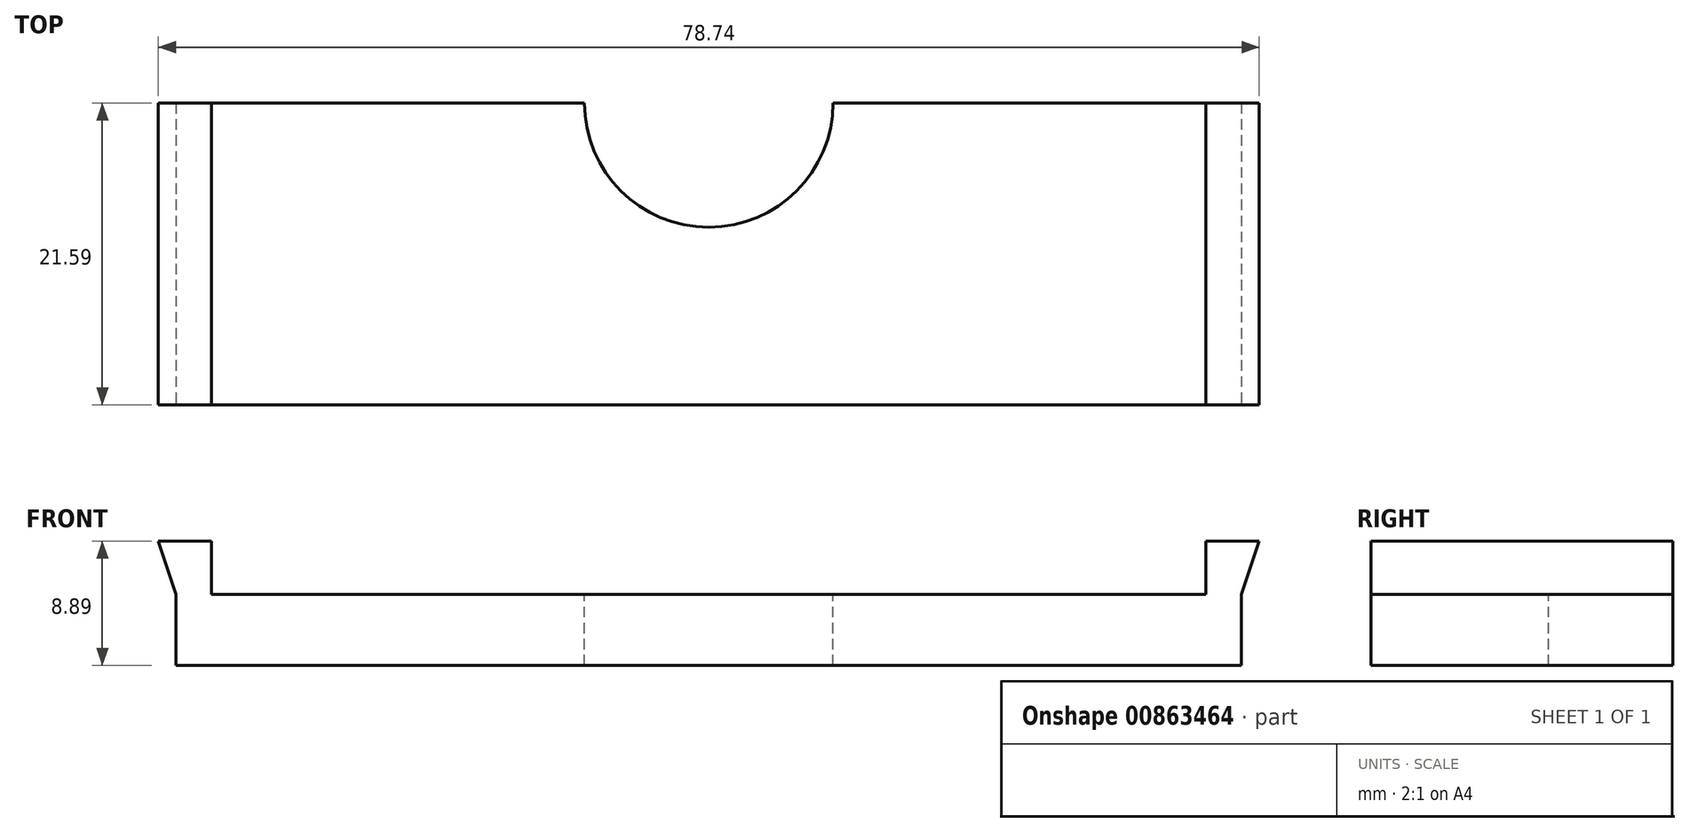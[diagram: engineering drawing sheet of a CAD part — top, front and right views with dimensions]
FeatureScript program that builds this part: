
annotation { "Feature Type Name" : "Feature", "Feature Type Description" : "" }
export const myFeature = defineFeature(function(context is Context, id is Id, definition is map)
    precondition{}
    {
        {
            var Q0;
            Q0=qCreatedBy(makeId("Top.planeOp"),FACE);
            var sketch = newSketch(context, id + "F0", { "sketchPlane" : qUnion([Q0])});
            skLineSegment(sketch, "E0.bottom", {"start": v(0, 0) * mm, "end": v(76.2, 0) * mm});
            skLineSegment(sketch, "E0.top", {"start": v(0, 21.59) * mm, "end": v(76.2, 21.59) * mm});
            skLineSegment(sketch, "E0.left", {"start": v(0, 0) * mm, "end": v(0, 21.59) * mm});
            skLineSegment(sketch, "E0.right", {"start": v(76.2, 0) * mm, "end": v(76.2, 21.59) * mm});
            skSolve(sketch);
        }
        {
            var Q0;
            Q0=makeQuery(id+"F0.imprint","IMPRINT",FACE,{"disambiguationData":[TD([[makeQuery(id+"F0.imprint","IMPRINT",EDGE,{"derivedFrom":sQuery(id+"F0.wireOp",EDGE,"E0.bottom")}),1.0]])]});
            extrude(context, id + "F1", {"entities" : qUnion([Q0]), "depth" : 5.08 * mm, "offsetDistance" : 25.4 * mm});
        }
        {
            var Q0;
            Q0=makeQuery(id+"F1.opExtrude","CAP_FACE",FACE,{"disambiguationData":[OSD([sQuery(id+"F0.wireOp",EDGE,"E0.bottom"),sQuery(id+"F0.wireOp",EDGE,"E0.top"),sQuery(id+"F0.wireOp",EDGE,"E0.left"),sQuery(id+"F0.wireOp",EDGE,"E0.right")])],"isStart":false});
            var sketch = newSketch(context, id + "F2", { "sketchPlane" : qUnion([Q0])});
            skLineSegment(sketch, "E1.bottom", {"start": v(76.2, 21.59) * mm, "end": v(73.66, 21.59) * mm});
            skLineSegment(sketch, "E1.top", {"start": v(76.2, 0) * mm, "end": v(73.66, 0) * mm});
            skLineSegment(sketch, "E1.left", {"start": v(76.2, 21.59) * mm, "end": v(76.2, 0) * mm});
            skLineSegment(sketch, "E1.right", {"start": v(73.66, 21.59) * mm, "end": v(73.66, 0) * mm});
            skLineSegment(sketch, "E2.bottom", {"start": v(0, 0) * mm, "end": v(2.54, 0) * mm});
            skLineSegment(sketch, "E2.top", {"start": v(0, 21.59) * mm, "end": v(2.54, 21.59) * mm});
            skLineSegment(sketch, "E2.left", {"start": v(0, 0) * mm, "end": v(0, 21.59) * mm});
            skLineSegment(sketch, "E2.right", {"start": v(2.54, 0) * mm, "end": v(2.54, 21.59) * mm});
            skSolve(sketch);
        }
        {
            var Q0;
            Q0=makeQuery(id+"F2.imprint","IMPRINT",FACE,{"disambiguationData":[TD([[makeQuery(id+"F2.imprint","IMPRINT",EDGE,{"derivedFrom":sQuery(id+"F2.wireOp",EDGE,"E2.bottom")}),1.0]])]});
            var Q1;
            Q1=makeQuery(id+"F2.imprint","IMPRINT",FACE,{"disambiguationData":[TD([[makeQuery(id+"F2.imprint","IMPRINT",EDGE,{"derivedFrom":sQuery(id+"F2.wireOp",EDGE,"E1.bottom")}),-1.0]])]});
            var Q2;
            Q2 = qSketchRegion(id + "F4", true);
            extrude(context, id + "F3", {"entities" : qUnion([Q0, Q1, Q2]), "operationType" : NewBodyOperationType.ADD, "depth" : 3.8 * mm, "offsetDistance" : 25.4 * mm});
        }
        {
            var Q0;
            Q0=makeQuery(id+"F1.opExtrude","CAP_FACE",FACE,{"disambiguationData":[OSD([sQuery(id+"F0.wireOp",EDGE,"E0.bottom"),sQuery(id+"F0.wireOp",EDGE,"E0.top"),sQuery(id+"F0.wireOp",EDGE,"E0.left"),sQuery(id+"F0.wireOp",EDGE,"E0.right")])],"isStart":false});
            var sketch = newSketch(context, id + "F4", { "sketchPlane" : qUnion([Q0])});
            skLineSegment(sketch, "E3", {"start": v(2.54, 10.8) * mm, "end": v(73.66, 10.8) * mm, "construction": true});
            skCircle(sketch, "E4", {"center": v(38.1, 21.59) * mm, "radius": 8.9 * mm});
            skSolve(sketch);
        }
        {
            var Q0;
            Q0=makeQuery(id+"F4.imprint","IMPRINT",FACE,{"disambiguationData":[TD([[makeQuery(id+"F4.imprint","IMPRINT",EDGE,{"derivedFrom":sQuery(id+"F4.wireOp",EDGE,"PgA4HHWj-m7D3-PoWC-p7U9-9KToe9dgFh9g")}),1.0]])]});
            var Q1;
            {var subQ0=sQuery(id+"F4.wireOp",EDGE,"E4");var subQ1=makeQuery(id+"F1.opExtrude","CAP_EDGE",EDGE,{"disambiguationData":[OSD([sQuery(id+"F0.wireOp",EDGE,"E0.top")])],"isStart":false});var subQ2=makeQuery(id+"F4.imprint","INTERSECT",VERTEX,{"disambiguationData":[OD(0.0)],"derivedFrom":[subQ1,subQ0]});Q1=makeQuery(id+"F4.imprint","IMPRINT",FACE,{"disambiguationData":[TD([[makeQuery(id+"F4.imprint","IMPRINT",EDGE,{"disambiguationData":[TD([[subQ2,-1.0]])],"derivedFrom":subQ0}),1.0]])]});}
            var Q2;
            {var subQ0=sQuery(id+"F4.wireOp",EDGE,"E4");var subQ1=makeQuery(id+"F1.opExtrude","CAP_EDGE",EDGE,{"disambiguationData":[OSD([sQuery(id+"F0.wireOp",EDGE,"E0.top")])],"isStart":false});var subQ2=makeQuery(id+"F4.imprint","INTERSECT",VERTEX,{"disambiguationData":[OD(0.0)],"derivedFrom":[subQ1,subQ0]});Q2=makeQuery(id+"F4.imprint","IMPRINT",FACE,{"disambiguationData":[TD([[makeQuery(id+"F4.imprint","IMPRINT",EDGE,{"disambiguationData":[TD([[subQ2,1.0]])],"derivedFrom":subQ0}),1.0]])]});}
            extrude(context, id + "F5", {"entities" : qUnion([Q0, Q1, Q2]), "operationType" : NewBodyOperationType.REMOVE, "oppositeDirection" : true, "depth" : 25.4 * mm, "offsetDistance" : 25.4 * mm});
        }
        {
            var Q0;
            Q0=makeQuery(id+"F3.boolean.opBoolean","MERGE",FACE,{"derivedFrom":[makeQuery(id+"F1.opExtrude","SWEPT_FACE",FACE,{"disambiguationData":[OSD([sQuery(id+"F0.wireOp",EDGE,"E0.bottom")])]}),makeQuery(id+"F3.opExtrude","SWEPT_FACE",FACE,{"disambiguationData":[OSD([sQuery(id+"F2.wireOp",EDGE,"E1.top")])]}),makeQuery(id+"F3.opExtrude","SWEPT_FACE",FACE,{"disambiguationData":[OSD([sQuery(id+"F2.wireOp",EDGE,"E2.bottom")])]})]});
            var sketch = newSketch(context, id + "F6", { "sketchPlane" : qUnion([Q0])});
            skLineSegment(sketch, "E5", {"start": v(0, 8.9) * mm, "end": v(-1.27, 8.9) * mm});
            skLineSegment(sketch, "E6", {"start": v(-1.27, 8.9) * mm, "end": v(0, 5.08) * mm});
            skLineSegment(sketch, "E7", {"start": v(0, 8.9) * mm, "end": v(0, 5.08) * mm});
            skLineSegment(sketch, "E8", {"start": v(76.2, 8.9) * mm, "end": v(77.47, 8.9) * mm});
            skLineSegment(sketch, "E9", {"start": v(77.47, 8.9) * mm, "end": v(76.2, 5.08) * mm});
            skLineSegment(sketch, "E10", {"start": v(76.2, 8.9) * mm, "end": v(76.2, 5.08) * mm});
            skSolve(sketch);
        }
        {
            var Q0;
            Q0=makeQuery(id+"F6.imprint","IMPRINT",FACE,{"disambiguationData":[TD([[makeQuery(id+"F6.imprint","IMPRINT",EDGE,{"derivedFrom":sQuery(id+"F6.wireOp",EDGE,"E5")}),1.0]])]});
            var Q1;
            Q1=makeQuery(id+"F6.imprint","IMPRINT",FACE,{"disambiguationData":[TD([[makeQuery(id+"F6.imprint","IMPRINT",EDGE,{"derivedFrom":sQuery(id+"F6.wireOp",EDGE,"E8")}),-1.0]])]});
            var Q2;
            Q2=makeQuery(id+"F3.boolean.opBoolean","MERGE",FACE,{"derivedFrom":[makeQuery(id+"F1.opExtrude","SWEPT_FACE",FACE,{"disambiguationData":[OSD([sQuery(id+"F0.wireOp",EDGE,"E0.top")])]}),makeQuery(id+"F3.opExtrude","SWEPT_FACE",FACE,{"disambiguationData":[OSD([sQuery(id+"F2.wireOp",EDGE,"E1.bottom")])]}),makeQuery(id+"F3.opExtrude","SWEPT_FACE",FACE,{"disambiguationData":[OSD([sQuery(id+"F2.wireOp",EDGE,"E2.top")])]})]});
            extrude(context, id + "F7", {"entities" : qUnion([Q0, Q1]), "operationType" : NewBodyOperationType.ADD, "endBound" : BoundingType.UP_TO_SURFACE, "oppositeDirection" : true, "depth" : 25.4 * mm, "endBoundEntityFace" : qUnion([Q2]), "offsetDistance" : 25.4 * mm});
        }
    });
